# Revit family: magiq_4_korona_810-0760
name_source: partatom
category: Leuchten
revit_build: Autodesk Revit 2016 (Build: 20190508_0715(x64)
units: mm (PartAtom-declared; Revit-internal decimal feet)

## family parameters
Basisbauteil = Fläche
Beim Laden mit Abzugskörper schneiden = Nein
Bemaßung runder Anschluss = Durchmesser verwenden
Gemeinsam genutzt = Nein
Lichtquelle = Nein
Raumberechnungspunkt = Nein
Teiletyp = Normal

## types (1)
- 810-0760-K10 (1 x LED, 880 lm, 13.3 W, 2700K)
    Beschreibung = MAGIQ 4 KORONA
    CIE Flux Codes = 100 100 100 100 73
    Color Rendering = 1A/90…99
    Color Temperature = 2700K
    Height = 56 mm  [stored 0.183727 ft]
    Hersteller = Prolicht
    Lamp Light Flux = 880 lm
    Lamp Power = 13.3 W
    Lamp count = 1
    Lampe = 1 x LED
    Length = 123 mm
    Luminous efficacy = 48 lm/W
    ModVariant = Nein
    Modell = 810-0760
    Mounting Place = Ceiling
    Mounting Type = Surface mounted
    Number of Poles = 1
    OnlyDefault = Ja
    Power Factor = 1
    Product Name = MAGIQ 4 KORONA
    Product group = Surface track spotlights
    ProductGroupID = 333
    Protection Class = Protection class
    Protection Degree = Degree of protection
    RLX_Detail_Level = 1
    RlxData = <blob elided: 317565 chars, md5=32ba617b>
    Scheinlast = 13 VA
    Socket = socket
    Standby Power = 0 W
    System Light Flux = 639 lm
    System Power = 13 W
    Typenbild = 810-0760.jpg
    Typenkommentare = REFLECTOR 10° (10)
    URL = http://relux.com
    VarID = 810-0760-k10
    Voltage = 0 V
    Vorgabe-Ansicht = 1800 mm
    Weight = 0.00 kg
    Width = 2475 mm

note: [stored X ft] marks values corroborated as IEEE doubles in the binary element streams (Revit-internal decimal feet)

## geometry (parser evidence)
native form markers: Blend x4, Sweep x12
no freeform markers — native parametric forms only
